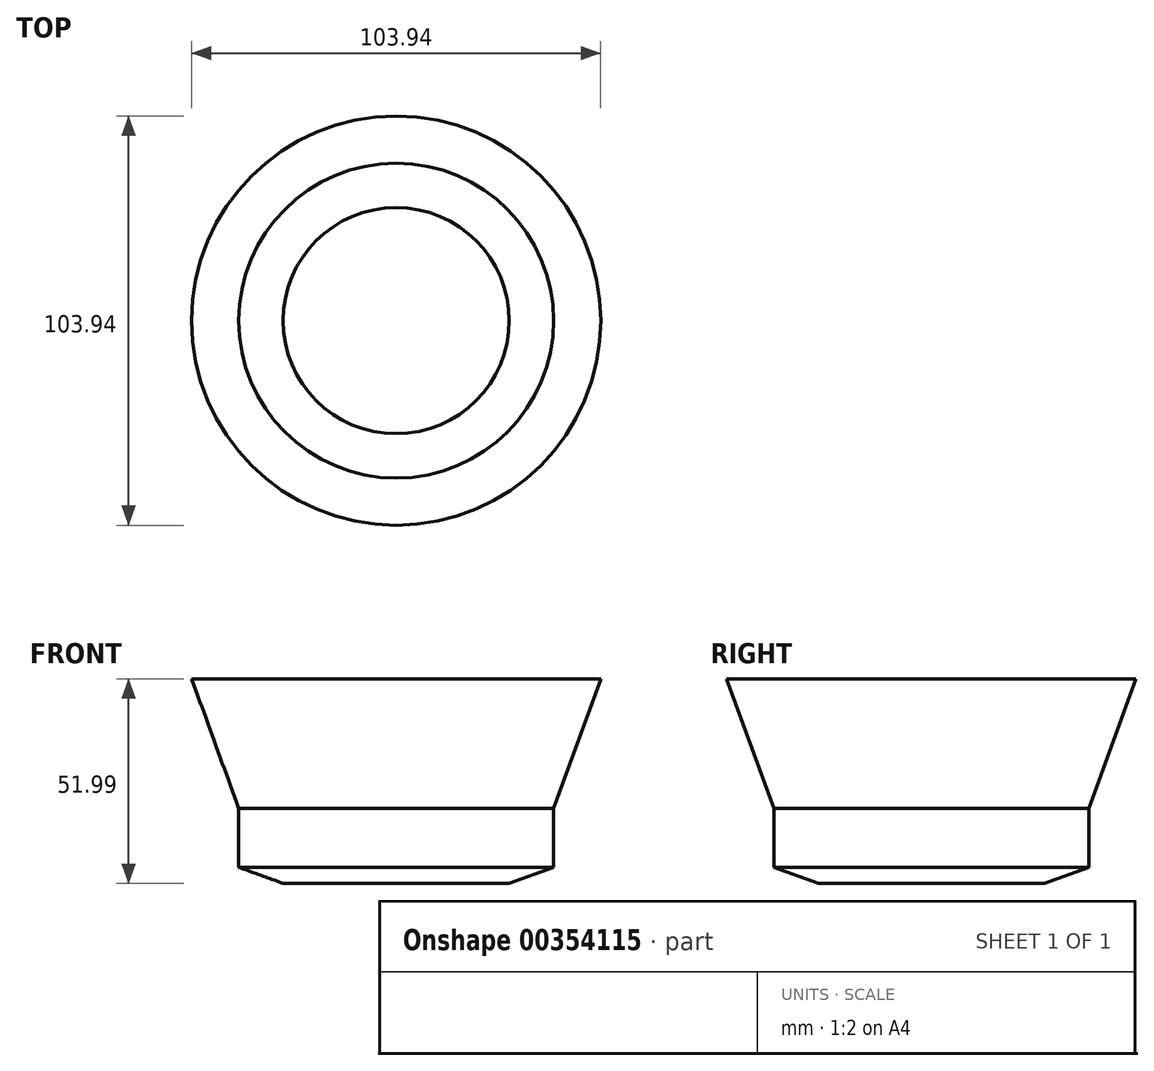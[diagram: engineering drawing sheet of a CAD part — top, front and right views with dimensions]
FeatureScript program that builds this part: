
annotation { "Feature Type Name" : "Feature", "Feature Type Description" : "" }
export const myFeature = defineFeature(function(context is Context, id is Id, definition is map)
    precondition{}
    {
        {
            var Q0;
            Q0=qCreatedBy(makeId("Front.planeOp"),FACE);
            var sketch = newSketch(context, id + "F0", { "sketchPlane" : qUnion([Q0])});
            skLineSegment(sketch, "E0", {"start": v(-40, 0) * mm, "end": v(-51.97, 32.89) * mm});
            skLineSegment(sketch, "E1", {"start": v(-40, 0) * mm, "end": v(-40, -15) * mm});
            skLineSegment(sketch, "E2", {"start": v(-40, -15) * mm, "end": v(-28.72, -19.1) * mm});
            skLineSegment(sketch, "E3", {"start": v(0, 83.6) * mm, "end": v(0, -53.1) * mm});
            skSolve(sketch);
        }
        {
            var Q0;
            Q0 = qSketchRegion(id + "F0", true);
            var Q1;
            Q1=sQuery(id+"F0.wireOp",EDGE,"E0");
            var Q2;
            Q2=sQuery(id+"F0.wireOp",EDGE,"E1");
            var Q3;
            Q3=sQuery(id+"F0.wireOp",EDGE,"E2");
            var Q4;
            Q4=sQuery(id+"F0.wireOp",EDGE,"E3");
            revolve(context, id + "F1", {"bodyType" : ToolBodyType.SURFACE, "entities" : qUnion([Q0]), "surfaceEntities" : qUnion([Q1, Q2, Q3]), "axis" : qUnion([Q4]), "revolveType" : RevolveType.FULL});
        }
    });
